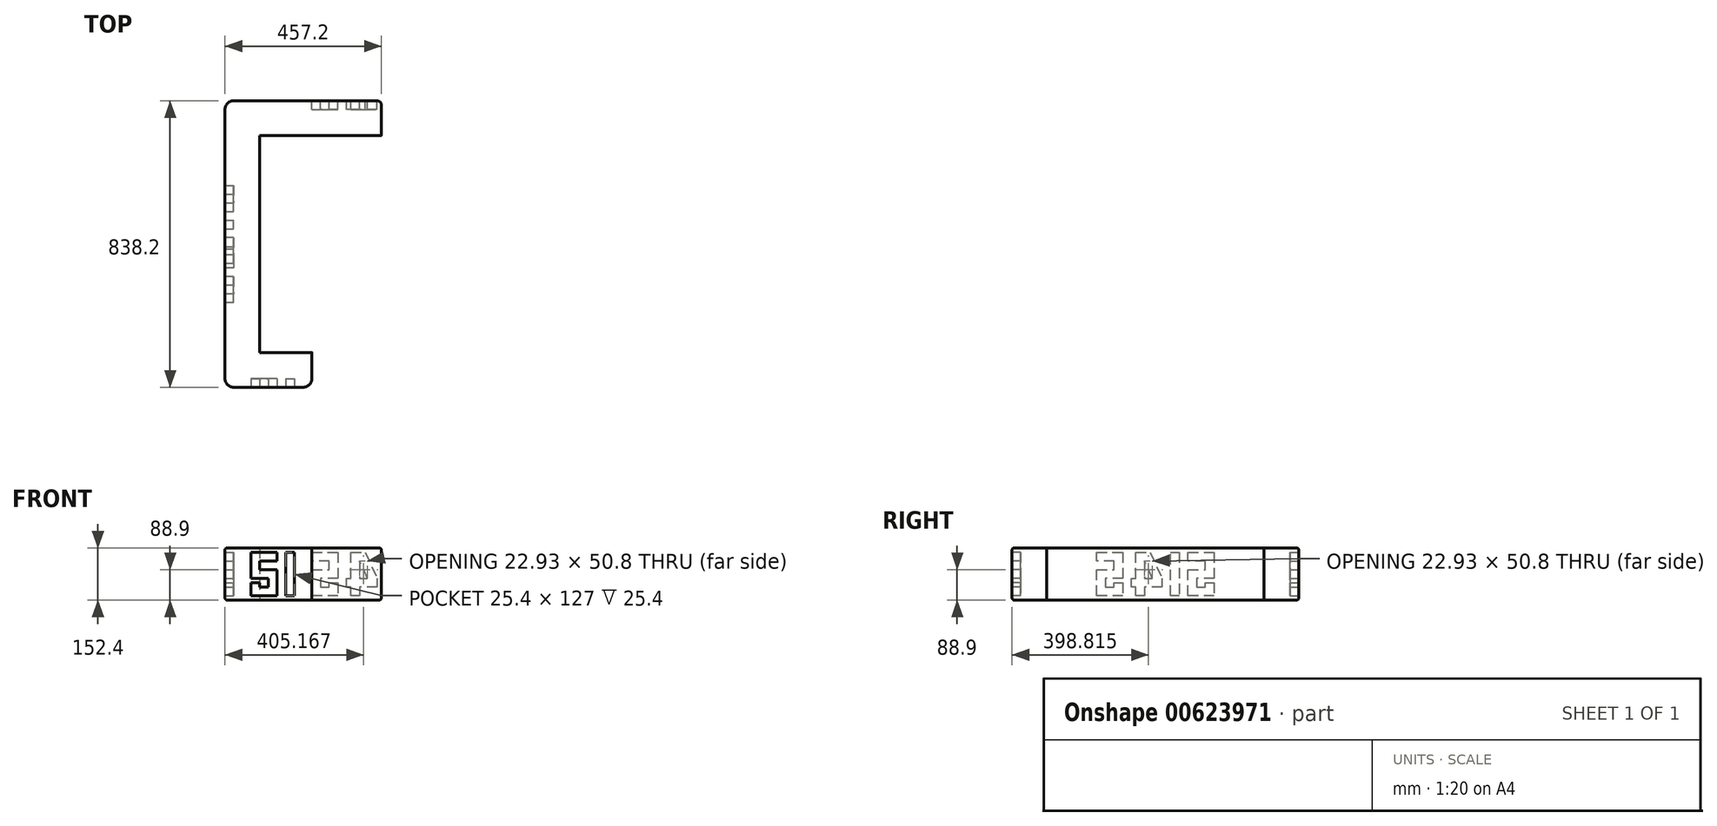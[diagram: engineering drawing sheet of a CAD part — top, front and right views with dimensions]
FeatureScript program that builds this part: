
annotation { "Feature Type Name" : "Feature", "Feature Type Description" : "" }
export const myFeature = defineFeature(function(context is Context, id is Id, definition is map)
    precondition{}
    {
        {
            var Q0;
            Q0=qCreatedBy(makeId("Top.planeOp"),FACE);
            var sketch = newSketch(context, id + "F0", { "sketchPlane" : qUnion([Q0])});
            skLineSegment(sketch, "E0", {"start": v(-101.57, 708.76) * mm, "end": v(-101.57, -129.44) * mm});
            skLineSegment(sketch, "E1", {"start": v(-101.57, -129.44) * mm, "end": v(152.43, -129.44) * mm});
            skLineSegment(sketch, "E2", {"start": v(152.43, -129.44) * mm, "end": v(152.43, -27.84) * mm});
            skLineSegment(sketch, "E3", {"start": v(152.43, -27.84) * mm, "end": v(0.03, -27.84) * mm});
            skLineSegment(sketch, "E4", {"start": v(0.03, -27.84) * mm, "end": v(0.03, 607.16) * mm});
            skLineSegment(sketch, "E5", {"start": v(0.03, 607.16) * mm, "end": v(355.63, 607.16) * mm});
            skLineSegment(sketch, "E6", {"start": v(355.63, 607.16) * mm, "end": v(355.63, 708.76) * mm});
            skLineSegment(sketch, "E7", {"start": v(355.63, 708.76) * mm, "end": v(-101.57, 708.76) * mm});
            skSolve(sketch);
        }
        {
            var Q0;
            Q0=makeQuery(id+"F0.imprint","IMPRINT",FACE,{"disambiguationData":[TD([[makeQuery(id+"F0.imprint","IMPRINT",EDGE,{"derivedFrom":sQuery(id+"F0.wireOp",EDGE,"E0")}),1.0]])]});
            extrude(context, id + "F1", {"entities" : qUnion([Q0]), "depth" : 152.4 * mm, "offsetDistance" : 25.4 * mm});
        }
        {
            var Q0;
            Q0=makeQuery(id+"F1.opExtrude","SWEPT_EDGE",EDGE,{"disambiguationData":[OSD([sQuery(id+"F0.wireOp",EDGE,"E0"),sQuery(id+"F0.wireOp",EDGE,"E1")])]});
            var Q1;
            Q1=makeQuery(id+"F1.opExtrude","SWEPT_EDGE",EDGE,{"disambiguationData":[OSD([sQuery(id+"F0.wireOp",EDGE,"E0"),sQuery(id+"F0.wireOp",EDGE,"E7")])]});
            var Q2;
            Q2=makeQuery(id+"F1.opExtrude","SWEPT_EDGE",EDGE,{"disambiguationData":[OSD([sQuery(id+"F0.wireOp",EDGE,"E1"),sQuery(id+"F0.wireOp",EDGE,"E2")])]});
            fillet(context, id + "F2", {"entities" : qUnion([Q0, Q1, Q2]), "radius" : 25.4 * mm, "tangentPropagation" : true, "allowEdgeOverflow" : false});
        }
        {
            var Q0;
            Q0=makeQuery(id+"F1.opExtrude","SWEPT_FACE",FACE,{"disambiguationData":[OSD([sQuery(id+"F0.wireOp",EDGE,"E0")])]});
            var sketch = newSketch(context, id + "F3", { "sketchPlane" : qUnion([Q0])});
            skLineSegment(sketch, "E8", {"start": v(-384.9, 139.7) * mm, "end": v(-461.1, 139.7) * mm});
            skLineSegment(sketch, "E9", {"start": v(-461.1, 139.7) * mm, "end": v(-461.1, 63.5) * mm});
            skLineSegment(sketch, "E10", {"start": v(-461.1, 63.5) * mm, "end": v(-410.3, 63.5) * mm});
            skLineSegment(sketch, "E11", {"start": v(-410.3, 63.5) * mm, "end": v(-410.3, 38.1) * mm});
            skLineSegment(sketch, "E12", {"start": v(-410.3, 38.1) * mm, "end": v(-435.7, 38.1) * mm});
            skLineSegment(sketch, "E13", {"start": v(-435.7, 38.1) * mm, "end": v(-435.7, 50.8) * mm});
            skLineSegment(sketch, "E14", {"start": v(-435.7, 50.8) * mm, "end": v(-461.1, 50.8) * mm});
            skLineSegment(sketch, "E15", {"start": v(-461.1, 50.8) * mm, "end": v(-461.1, 12.7) * mm});
            skLineSegment(sketch, "E16", {"start": v(-461.1, 12.7) * mm, "end": v(-384.9, 12.7) * mm});
            skLineSegment(sketch, "E17", {"start": v(-384.9, 12.7) * mm, "end": v(-384.9, 88.9) * mm});
            skLineSegment(sketch, "E18", {"start": v(-384.9, 88.9) * mm, "end": v(-435.7, 88.9) * mm});
            skLineSegment(sketch, "E19", {"start": v(-435.7, 88.9) * mm, "end": v(-435.7, 114.3) * mm});
            skLineSegment(sketch, "E20", {"start": v(-435.7, 114.3) * mm, "end": v(-384.9, 114.3) * mm});
            skLineSegment(sketch, "E21", {"start": v(-384.9, 114.3) * mm, "end": v(-384.9, 139.7) * mm});
            skLineSegment(sketch, "E22", {"start": v(-359.5, 139.7) * mm, "end": v(-359.5, 12.7) * mm});
            skLineSegment(sketch, "E23", {"start": v(-359.5, 12.7) * mm, "end": v(-334.1, 12.7) * mm});
            skLineSegment(sketch, "E24", {"start": v(-334.1, 12.7) * mm, "end": v(-334.1, 139.7) * mm});
            skLineSegment(sketch, "E25", {"start": v(-334.1, 139.7) * mm, "end": v(-359.5, 139.7) * mm});
            skLineSegment(sketch, "E26", {"start": v(-274.31, 139.7) * mm, "end": v(-308.7, 63.5) * mm});
            skLineSegment(sketch, "E27", {"start": v(-308.7, 63.5) * mm, "end": v(-308.7, 38.1) * mm});
            skLineSegment(sketch, "E28", {"start": v(-308.7, 38.1) * mm, "end": v(-257.9, 38.1) * mm});
            skLineSegment(sketch, "E29", {"start": v(-257.9, 38.1) * mm, "end": v(-257.9, 12.7) * mm});
            skLineSegment(sketch, "E30", {"start": v(-257.9, 12.7) * mm, "end": v(-232.5, 12.7) * mm});
            skLineSegment(sketch, "E31", {"start": v(-232.5, 12.7) * mm, "end": v(-232.5, 38.1) * mm});
            skLineSegment(sketch, "E32", {"start": v(-232.5, 38.1) * mm, "end": v(-219.8, 38.1) * mm});
            skLineSegment(sketch, "E33", {"start": v(-219.8, 38.1) * mm, "end": v(-219.8, 63.5) * mm});
            skLineSegment(sketch, "E34", {"start": v(-219.8, 63.5) * mm, "end": v(-232.5, 63.5) * mm});
            skLineSegment(sketch, "E35", {"start": v(-232.5, 63.5) * mm, "end": v(-232.5, 139.7) * mm});
            skLineSegment(sketch, "E36", {"start": v(-232.5, 139.7) * mm, "end": v(-274.31, 139.7) * mm});
            skLineSegment(sketch, "E37", {"start": v(-257.9, 63.5) * mm, "end": v(-280.84, 63.5) * mm});
            skLineSegment(sketch, "E38", {"start": v(-280.84, 63.5) * mm, "end": v(-257.9, 114.3) * mm});
            skLineSegment(sketch, "E39", {"start": v(-257.9, 114.3) * mm, "end": v(-257.9, 63.5) * mm});
            skLineSegment(sketch, "E40", {"start": v(-118.2, 139.7) * mm, "end": v(-194.4, 139.7) * mm});
            skLineSegment(sketch, "E41", {"start": v(-194.4, 139.7) * mm, "end": v(-194.4, 63.5) * mm});
            skPoint(sketch, "E41.endSnap0", {"position": v(-257.9, 88.9) * mm});
            skLineSegment(sketch, "E42", {"start": v(-194.4, 63.5) * mm, "end": v(-143.6, 63.5) * mm});
            skLineSegment(sketch, "E43", {"start": v(-143.6, 63.5) * mm, "end": v(-143.6, 38.1) * mm});
            skLineSegment(sketch, "E44", {"start": v(-143.6, 38.1) * mm, "end": v(-169, 38.1) * mm});
            skLineSegment(sketch, "E45", {"start": v(-169, 38.1) * mm, "end": v(-169, 50.8) * mm});
            skLineSegment(sketch, "E46", {"start": v(-169, 50.8) * mm, "end": v(-194.4, 50.8) * mm});
            skLineSegment(sketch, "E47", {"start": v(-194.4, 50.8) * mm, "end": v(-194.4, 12.7) * mm});
            skLineSegment(sketch, "E48", {"start": v(-194.4, 12.7) * mm, "end": v(-118.2, 12.7) * mm});
            skLineSegment(sketch, "E49", {"start": v(-118.2, 12.7) * mm, "end": v(-118.2, 88.9) * mm});
            skLineSegment(sketch, "E50", {"start": v(-118.2, 88.9) * mm, "end": v(-169, 88.9) * mm});
            skLineSegment(sketch, "E51", {"start": v(-169, 88.9) * mm, "end": v(-169, 114.3) * mm});
            skLineSegment(sketch, "E52", {"start": v(-169, 114.3) * mm, "end": v(-118.2, 114.3) * mm});
            skLineSegment(sketch, "E53", {"start": v(-118.2, 114.3) * mm, "end": v(-118.2, 139.7) * mm});
            skLineSegment(sketch, "E54", {"start": v(-461.1, 139.7) * mm, "end": v(-683.36, 139.7) * mm});
            skLineSegment(sketch, "E55", {"start": v(-118.2, 139.7) * mm, "end": v(104.04, 139.7) * mm});
            skSolve(sketch);
        }
        {
            var Q0;
            Q0=makeQuery(id+"F3.imprint","IMPRINT",FACE,{"disambiguationData":[TD([[makeQuery(id+"F3.imprint","IMPRINT",EDGE,{"derivedFrom":sQuery(id+"F3.wireOp",EDGE,"E8")}),1.0]])]});
            var Q1;
            Q1=makeQuery(id+"F3.imprint","IMPRINT",FACE,{"disambiguationData":[TD([[makeQuery(id+"F3.imprint","IMPRINT",EDGE,{"derivedFrom":sQuery(id+"F3.wireOp",EDGE,"E22")}),1.0]])]});
            var Q2;
            Q2=makeQuery(id+"F3.imprint","IMPRINT",FACE,{"disambiguationData":[TD([[makeQuery(id+"F3.imprint","IMPRINT",EDGE,{"derivedFrom":sQuery(id+"F3.wireOp",EDGE,"E26")}),1.0]])]});
            var Q3;
            Q3=makeQuery(id+"F3.imprint","IMPRINT",FACE,{"disambiguationData":[TD([[makeQuery(id+"F3.imprint","IMPRINT",EDGE,{"derivedFrom":sQuery(id+"F3.wireOp",EDGE,"E40")}),1.0]])]});
            extrude(context, id + "F4", {"entities" : qUnion([Q0, Q1, Q2, Q3]), "operationType" : NewBodyOperationType.REMOVE, "oppositeDirection" : true, "depth" : 25.4 * mm, "offsetDistance" : 25.4 * mm});
        }
        {
            var Q0;
            Q0=makeQuery(id+"F4.boolean.opBoolean","COPY",FACE,{"derivedFrom":makeQuery(id+"F4.opExtrude","CAP_FACE",FACE,{"disambiguationData":[OSD([sQuery(id+"F3.wireOp",EDGE,"E8"),sQuery(id+"F3.wireOp",EDGE,"E9"),sQuery(id+"F3.wireOp",EDGE,"E10"),sQuery(id+"F3.wireOp",EDGE,"E11"),sQuery(id+"F3.wireOp",EDGE,"E12"),sQuery(id+"F3.wireOp",EDGE,"E13"),sQuery(id+"F3.wireOp",EDGE,"E14"),sQuery(id+"F3.wireOp",EDGE,"E15"),sQuery(id+"F3.wireOp",EDGE,"E16"),sQuery(id+"F3.wireOp",EDGE,"E17"),sQuery(id+"F3.wireOp",EDGE,"E18"),sQuery(id+"F3.wireOp",EDGE,"E19"),sQuery(id+"F3.wireOp",EDGE,"E20"),sQuery(id+"F3.wireOp",EDGE,"E21")])],"isStart":false})});
            var Q1;
            Q1=makeQuery(id+"F4.boolean.opBoolean","COPY",FACE,{"derivedFrom":makeQuery(id+"F4.opExtrude","CAP_FACE",FACE,{"disambiguationData":[OSD([sQuery(id+"F3.wireOp",EDGE,"E22"),sQuery(id+"F3.wireOp",EDGE,"E23"),sQuery(id+"F3.wireOp",EDGE,"E24"),sQuery(id+"F3.wireOp",EDGE,"E25")])],"isStart":false})});
            var Q2;
            Q2=makeQuery(id+"F4.boolean.opBoolean","COPY",FACE,{"derivedFrom":makeQuery(id+"F4.opExtrude","CAP_FACE",FACE,{"disambiguationData":[OSD([sQuery(id+"F3.wireOp",EDGE,"E26"),sQuery(id+"F3.wireOp",EDGE,"E27"),sQuery(id+"F3.wireOp",EDGE,"E28"),sQuery(id+"F3.wireOp",EDGE,"E29"),sQuery(id+"F3.wireOp",EDGE,"E30"),sQuery(id+"F3.wireOp",EDGE,"E31"),sQuery(id+"F3.wireOp",EDGE,"E32"),sQuery(id+"F3.wireOp",EDGE,"E33"),sQuery(id+"F3.wireOp",EDGE,"E34"),sQuery(id+"F3.wireOp",EDGE,"E35"),sQuery(id+"F3.wireOp",EDGE,"E36"),sQuery(id+"F3.wireOp",EDGE,"E37"),sQuery(id+"F3.wireOp",EDGE,"E38"),sQuery(id+"F3.wireOp",EDGE,"E39")])],"isStart":false})});
            var Q3;
            Q3=makeQuery(id+"F4.boolean.opBoolean","COPY",FACE,{"derivedFrom":makeQuery(id+"F4.opExtrude","CAP_FACE",FACE,{"disambiguationData":[OSD([sQuery(id+"F3.wireOp",EDGE,"E40"),sQuery(id+"F3.wireOp",EDGE,"E41"),sQuery(id+"F3.wireOp",EDGE,"E42"),sQuery(id+"F3.wireOp",EDGE,"E43"),sQuery(id+"F3.wireOp",EDGE,"E44"),sQuery(id+"F3.wireOp",EDGE,"E45"),sQuery(id+"F3.wireOp",EDGE,"E46"),sQuery(id+"F3.wireOp",EDGE,"E47"),sQuery(id+"F3.wireOp",EDGE,"E48"),sQuery(id+"F3.wireOp",EDGE,"E49"),sQuery(id+"F3.wireOp",EDGE,"E50"),sQuery(id+"F3.wireOp",EDGE,"E51"),sQuery(id+"F3.wireOp",EDGE,"E52"),sQuery(id+"F3.wireOp",EDGE,"E53")])],"isStart":false})});
            extrude(context, id + "F5", {"entities" : qUnion([Q0, Q1, Q2, Q3]), "depth" : 25.4 * mm, "offsetDistance" : 25.4 * mm});
        }
        {
            var Q0;
            Q0=makeQuery(id+"F1.opExtrude","SWEPT_FACE",FACE,{"disambiguationData":[OSD([sQuery(id+"F0.wireOp",EDGE,"E1")])]});
            var sketch = newSketch(context, id + "F6", { "sketchPlane" : qUnion([Q0])});
            skLineSegment(sketch, "E56", {"start": v(50.83, 139.7) * mm, "end": v(-25.37, 139.7) * mm});
            skLineSegment(sketch, "E57", {"start": v(-25.37, 139.7) * mm, "end": v(-25.37, 63.5) * mm});
            skLineSegment(sketch, "E58", {"start": v(-25.37, 63.5) * mm, "end": v(25.43, 63.5) * mm});
            skLineSegment(sketch, "E59", {"start": v(25.43, 63.5) * mm, "end": v(25.43, 38.1) * mm});
            skLineSegment(sketch, "E60", {"start": v(25.43, 38.1) * mm, "end": v(0.03, 38.1) * mm});
            skLineSegment(sketch, "E61", {"start": v(0.03, 38.1) * mm, "end": v(0.03, 50.8) * mm});
            skLineSegment(sketch, "E62", {"start": v(0.03, 50.8) * mm, "end": v(-25.37, 50.8) * mm});
            skLineSegment(sketch, "E63", {"start": v(-25.37, 50.8) * mm, "end": v(-25.37, 12.7) * mm});
            skLineSegment(sketch, "E64", {"start": v(-25.37, 12.7) * mm, "end": v(50.83, 12.7) * mm});
            skLineSegment(sketch, "E65", {"start": v(50.83, 12.7) * mm, "end": v(50.83, 88.9) * mm});
            skLineSegment(sketch, "E66", {"start": v(50.83, 88.9) * mm, "end": v(0.03, 88.9) * mm});
            skLineSegment(sketch, "E67", {"start": v(0.03, 88.9) * mm, "end": v(0.03, 114.3) * mm});
            skLineSegment(sketch, "E68", {"start": v(0.03, 114.3) * mm, "end": v(50.83, 114.3) * mm});
            skLineSegment(sketch, "E69", {"start": v(50.83, 114.3) * mm, "end": v(50.83, 139.7) * mm});
            skLineSegment(sketch, "E70", {"start": v(76.23, 139.7) * mm, "end": v(101.63, 139.7) * mm});
            skLineSegment(sketch, "E71", {"start": v(101.63, 139.7) * mm, "end": v(101.63, 12.7) * mm});
            skLineSegment(sketch, "E72", {"start": v(101.63, 12.7) * mm, "end": v(76.23, 12.7) * mm});
            skLineSegment(sketch, "E73", {"start": v(76.23, 12.7) * mm, "end": v(76.23, 139.7) * mm});
            skSolve(sketch);
        }
        {
            var Q0;
            Q0=makeQuery(id+"F6.imprint","IMPRINT",FACE,{"disambiguationData":[TD([[makeQuery(id+"F6.imprint","IMPRINT",EDGE,{"derivedFrom":sQuery(id+"F6.wireOp",EDGE,"E56")}),1.0]])]});
            var Q1;
            Q1=makeQuery(id+"F6.imprint","IMPRINT",FACE,{"disambiguationData":[TD([[makeQuery(id+"F6.imprint","IMPRINT",EDGE,{"derivedFrom":sQuery(id+"F6.wireOp",EDGE,"E70")}),-1.0]])]});
            extrude(context, id + "F7", {"entities" : qUnion([Q0, Q1]), "operationType" : NewBodyOperationType.REMOVE, "oppositeDirection" : true, "depth" : 25.4 * mm, "offsetDistance" : 25.4 * mm});
        }
        {
            var Q0;
            Q0=makeQuery(id+"F7.boolean.opBoolean","COPY",FACE,{"derivedFrom":makeQuery(id+"F7.opExtrude","CAP_FACE",FACE,{"disambiguationData":[OSD([sQuery(id+"F6.wireOp",EDGE,"E56"),sQuery(id+"F6.wireOp",EDGE,"E57"),sQuery(id+"F6.wireOp",EDGE,"E58"),sQuery(id+"F6.wireOp",EDGE,"E59"),sQuery(id+"F6.wireOp",EDGE,"E60"),sQuery(id+"F6.wireOp",EDGE,"E61"),sQuery(id+"F6.wireOp",EDGE,"E62"),sQuery(id+"F6.wireOp",EDGE,"E63"),sQuery(id+"F6.wireOp",EDGE,"E64"),sQuery(id+"F6.wireOp",EDGE,"E65"),sQuery(id+"F6.wireOp",EDGE,"E66"),sQuery(id+"F6.wireOp",EDGE,"E67"),sQuery(id+"F6.wireOp",EDGE,"E68"),sQuery(id+"F6.wireOp",EDGE,"E69")])],"isStart":false})});
            var Q1;
            Q1=makeQuery(id+"F7.boolean.opBoolean","COPY",FACE,{"derivedFrom":makeQuery(id+"F7.opExtrude","CAP_FACE",FACE,{"disambiguationData":[OSD([sQuery(id+"F6.wireOp",EDGE,"E70"),sQuery(id+"F6.wireOp",EDGE,"E71"),sQuery(id+"F6.wireOp",EDGE,"E72"),sQuery(id+"F6.wireOp",EDGE,"E73")])],"isStart":false})});
            extrude(context, id + "F8", {"entities" : qUnion([Q0, Q1]), "depth" : 25.4 * mm, "offsetDistance" : 25.4 * mm});
        }
        {
            var Q0;
            Q0=makeQuery(id+"F1.opExtrude","SWEPT_FACE",FACE,{"disambiguationData":[OSD([sQuery(id+"F0.wireOp",EDGE,"E7")])]});
            var sketch = newSketch(context, id + "F9", { "sketchPlane" : qUnion([Q0])});
            skLineSegment(sketch, "E74", {"start": v(-308.53, 139.7) * mm, "end": v(-342.93, 63.5) * mm});
            skLineSegment(sketch, "E75", {"start": v(-342.93, 63.5) * mm, "end": v(-342.93, 38.1) * mm});
            skLineSegment(sketch, "E76", {"start": v(-342.93, 38.1) * mm, "end": v(-292.13, 38.1) * mm});
            skLineSegment(sketch, "E77", {"start": v(-292.13, 38.1) * mm, "end": v(-292.13, 12.7) * mm});
            skLineSegment(sketch, "E78", {"start": v(-292.13, 12.7) * mm, "end": v(-266.73, 12.7) * mm});
            skLineSegment(sketch, "E79", {"start": v(-266.73, 12.7) * mm, "end": v(-266.73, 38.1) * mm});
            skLineSegment(sketch, "E80", {"start": v(-266.73, 38.1) * mm, "end": v(-254.03, 38.1) * mm});
            skLineSegment(sketch, "E81", {"start": v(-254.03, 38.1) * mm, "end": v(-254.03, 63.5) * mm});
            skLineSegment(sketch, "E82", {"start": v(-254.03, 63.5) * mm, "end": v(-266.73, 63.5) * mm});
            skLineSegment(sketch, "E83", {"start": v(-266.73, 63.5) * mm, "end": v(-266.73, 139.7) * mm});
            skLineSegment(sketch, "E84", {"start": v(-266.73, 139.7) * mm, "end": v(-308.53, 139.7) * mm});
            skLineSegment(sketch, "E85", {"start": v(-315.06, 63.5) * mm, "end": v(-292.13, 114.3) * mm});
            skLineSegment(sketch, "E86", {"start": v(-292.13, 114.3) * mm, "end": v(-292.13, 63.5) * mm});
            skLineSegment(sketch, "E87", {"start": v(-292.13, 63.5) * mm, "end": v(-315.06, 63.5) * mm});
            skLineSegment(sketch, "E88", {"start": v(-152.43, 139.7) * mm, "end": v(-228.63, 139.7) * mm});
            skLineSegment(sketch, "E89", {"start": v(-228.63, 139.7) * mm, "end": v(-228.63, 63.5) * mm});
            skLineSegment(sketch, "E90", {"start": v(-228.63, 63.5) * mm, "end": v(-177.83, 63.5) * mm});
            skLineSegment(sketch, "E91", {"start": v(-177.83, 63.5) * mm, "end": v(-177.83, 38.1) * mm});
            skLineSegment(sketch, "E92", {"start": v(-177.83, 38.1) * mm, "end": v(-203.23, 38.1) * mm});
            skLineSegment(sketch, "E93", {"start": v(-203.23, 38.1) * mm, "end": v(-203.23, 50.8) * mm});
            skLineSegment(sketch, "E94", {"start": v(-203.23, 50.8) * mm, "end": v(-228.63, 50.8) * mm});
            skLineSegment(sketch, "E95", {"start": v(-228.63, 50.8) * mm, "end": v(-228.63, 12.7) * mm});
            skLineSegment(sketch, "E96", {"start": v(-228.63, 12.7) * mm, "end": v(-152.43, 12.7) * mm});
            skLineSegment(sketch, "E97", {"start": v(-152.43, 12.7) * mm, "end": v(-152.43, 88.9) * mm});
            skLineSegment(sketch, "E98", {"start": v(-152.43, 88.9) * mm, "end": v(-203.23, 88.9) * mm});
            skLineSegment(sketch, "E99", {"start": v(-203.23, 88.9) * mm, "end": v(-203.23, 114.3) * mm});
            skLineSegment(sketch, "E100", {"start": v(-203.23, 114.3) * mm, "end": v(-152.43, 114.3) * mm});
            skLineSegment(sketch, "E101", {"start": v(-152.43, 114.3) * mm, "end": v(-152.43, 139.7) * mm});
            skSolve(sketch);
        }
        {
            var Q0;
            Q0=makeQuery(id+"F9.imprint","IMPRINT",FACE,{"disambiguationData":[TD([[makeQuery(id+"F9.imprint","IMPRINT",EDGE,{"derivedFrom":sQuery(id+"F9.wireOp",EDGE,"E74")}),1.0]])]});
            var Q1;
            Q1=makeQuery(id+"F9.imprint","IMPRINT",FACE,{"disambiguationData":[TD([[makeQuery(id+"F9.imprint","IMPRINT",EDGE,{"derivedFrom":sQuery(id+"F9.wireOp",EDGE,"E88")}),1.0]])]});
            extrude(context, id + "F10", {"entities" : qUnion([Q0, Q1]), "operationType" : NewBodyOperationType.REMOVE, "oppositeDirection" : true, "depth" : 25.4 * mm, "offsetDistance" : 25.4 * mm});
        }
        {
            var Q0;
            Q0=makeQuery(id+"F10.boolean.opBoolean","COPY",FACE,{"derivedFrom":makeQuery(id+"F10.opExtrude","CAP_FACE",FACE,{"disambiguationData":[OSD([sQuery(id+"F9.wireOp",EDGE,"E74"),sQuery(id+"F9.wireOp",EDGE,"E75"),sQuery(id+"F9.wireOp",EDGE,"E76"),sQuery(id+"F9.wireOp",EDGE,"E77"),sQuery(id+"F9.wireOp",EDGE,"E78"),sQuery(id+"F9.wireOp",EDGE,"E79"),sQuery(id+"F9.wireOp",EDGE,"E80"),sQuery(id+"F9.wireOp",EDGE,"E81"),sQuery(id+"F9.wireOp",EDGE,"E82"),sQuery(id+"F9.wireOp",EDGE,"E83"),sQuery(id+"F9.wireOp",EDGE,"E84"),sQuery(id+"F9.wireOp",EDGE,"E85"),sQuery(id+"F9.wireOp",EDGE,"E86"),sQuery(id+"F9.wireOp",EDGE,"E87")])],"isStart":false})});
            var Q1;
            Q1=makeQuery(id+"F10.boolean.opBoolean","COPY",FACE,{"derivedFrom":makeQuery(id+"F10.opExtrude","CAP_FACE",FACE,{"disambiguationData":[OSD([sQuery(id+"F9.wireOp",EDGE,"E88"),sQuery(id+"F9.wireOp",EDGE,"E89"),sQuery(id+"F9.wireOp",EDGE,"E90"),sQuery(id+"F9.wireOp",EDGE,"E91"),sQuery(id+"F9.wireOp",EDGE,"E92"),sQuery(id+"F9.wireOp",EDGE,"E93"),sQuery(id+"F9.wireOp",EDGE,"E94"),sQuery(id+"F9.wireOp",EDGE,"E95"),sQuery(id+"F9.wireOp",EDGE,"E96"),sQuery(id+"F9.wireOp",EDGE,"E97"),sQuery(id+"F9.wireOp",EDGE,"E98"),sQuery(id+"F9.wireOp",EDGE,"E99"),sQuery(id+"F9.wireOp",EDGE,"E100"),sQuery(id+"F9.wireOp",EDGE,"E101")])],"isStart":false})});
            extrude(context, id + "F11", {"entities" : qUnion([Q0, Q1]), "depth" : 25.4 * mm, "offsetDistance" : 25.4 * mm});
        }
        {
            var Q0;
            Q0=makeQuery(id+"F1.opExtrude","SWEPT_EDGE",EDGE,{"disambiguationData":[OSD([sQuery(id+"F0.wireOp",EDGE,"E6"),sQuery(id+"F0.wireOp",EDGE,"E7")])]});
            fillet(context, id + "F12", {"entities" : qUnion([Q0]), "radius" : 12.7 * mm, "tangentPropagation" : true, "allowEdgeOverflow" : false});
        }
        {
            var Q0;
            Q0=makeQuery(id+"F1.opExtrude","CAP_EDGE",EDGE,{"disambiguationData":[OSD([sQuery(id+"F0.wireOp",EDGE,"E0")])],"isStart":false});
            var Q1;
            Q1=makeQuery(id+"F1.opExtrude","CAP_EDGE",EDGE,{"disambiguationData":[OSD([sQuery(id+"F0.wireOp",EDGE,"E0")])],"isStart":true});
            fillet(context, id + "F13", {"entities" : qUnion([Q0, Q1]), "radius" : 6.35 * mm, "tangentPropagation" : true, "allowEdgeOverflow" : false});
        }
    });
